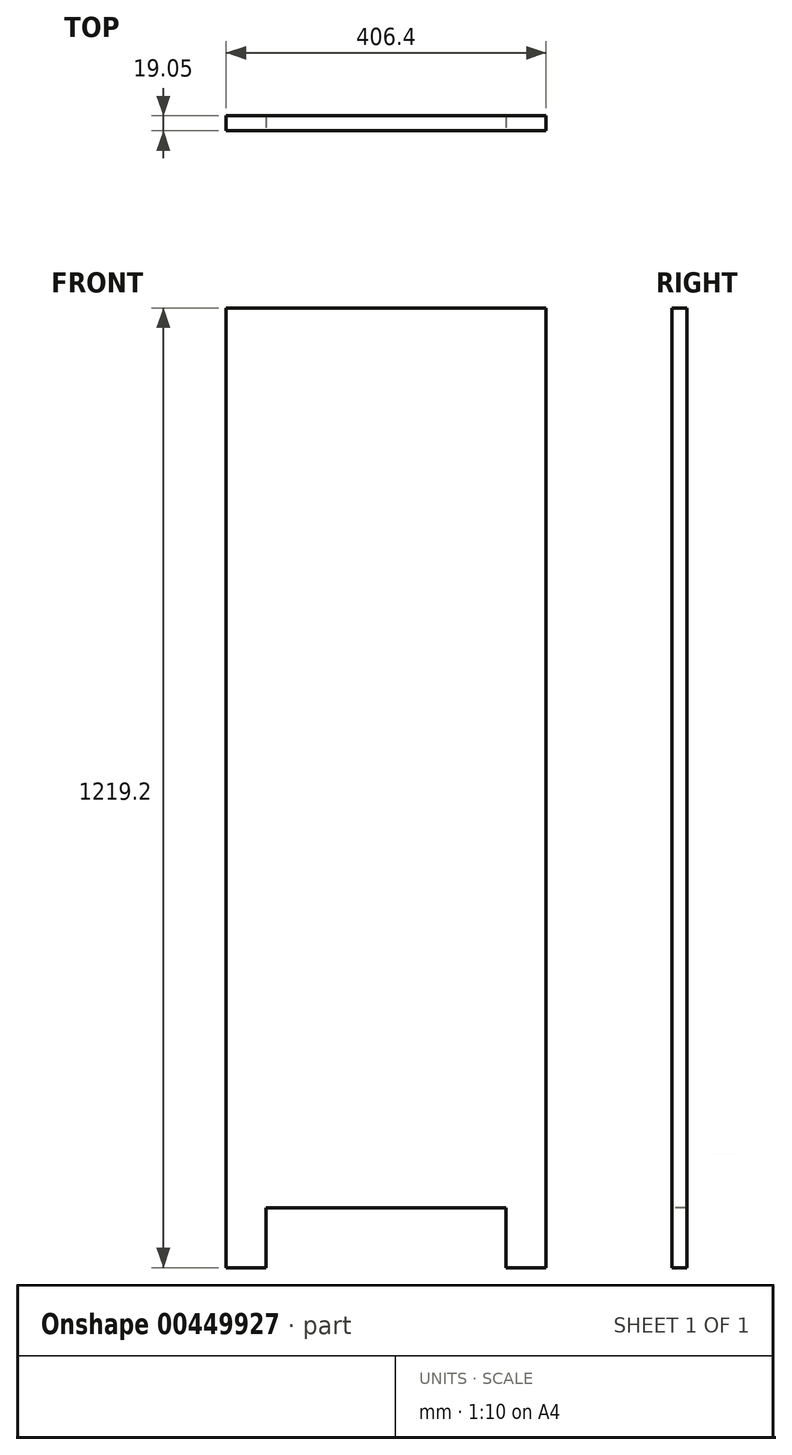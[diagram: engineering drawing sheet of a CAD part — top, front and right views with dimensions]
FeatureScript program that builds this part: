
annotation { "Feature Type Name" : "Feature", "Feature Type Description" : "" }
export const myFeature = defineFeature(function(context is Context, id is Id, definition is map)
    precondition{}
    {
        {
            var Q0;
            Q0=qCreatedBy(makeId("Top.planeOp"),FACE);
            var sketch = newSketch(context, id + "F0", { "sketchPlane" : qUnion([Q0])});
            skLineSegment(sketch, "E0.bottom", {"start": v(0, 0) * mm, "end": v(406.4, 0) * mm});
            skLineSegment(sketch, "E0.top", {"start": v(0, 19.05) * mm, "end": v(406.4, 19.05) * mm});
            skLineSegment(sketch, "E0.left", {"start": v(0, 0) * mm, "end": v(0, 19.05) * mm});
            skLineSegment(sketch, "E0.right", {"start": v(406.4, 0) * mm, "end": v(406.4, 19.05) * mm});
            skSolve(sketch);
        }
        {
            var Q0;
            Q0=makeQuery(id+"F0.imprint","IMPRINT",FACE,{"disambiguationData":[TD([[makeQuery(id+"F0.imprint","IMPRINT",EDGE,{"derivedFrom":sQuery(id+"F0.wireOp",EDGE,"E0.bottom")}),1.0]])]});
            extrude(context, id + "F1", {"entities" : qUnion([Q0]), "depth" : 1219.2 * mm});
        }
        {
            var Q0;
            Q0=makeQuery(id+"F1.opExtrude","SWEPT_FACE",FACE,{"disambiguationData":[OSD([sQuery(id+"F0.wireOp",EDGE,"E0.bottom")])]});
            var sketch = newSketch(context, id + "F2", { "sketchPlane" : qUnion([Q0])});
            skLineSegment(sketch, "E1.bottom", {"start": v(50.8, 0) * mm, "end": v(355.6, 0) * mm});
            skLineSegment(sketch, "E1.top", {"start": v(50.8, 76.2) * mm, "end": v(355.6, 76.2) * mm});
            skLineSegment(sketch, "E1.left", {"start": v(50.8, 0) * mm, "end": v(50.8, 76.2) * mm});
            skLineSegment(sketch, "E1.right", {"start": v(355.6, 0) * mm, "end": v(355.6, 76.2) * mm});
            skLineSegment(sketch, "E2", {"start": v(203.2, 76.2) * mm, "end": v(203.2, 0) * mm, "construction": true});
            skSolve(sketch);
        }
        {
            var Q0;
            Q0=makeQuery(id+"F2.imprint","IMPRINT",FACE,{"disambiguationData":[TD([[makeQuery(id+"F2.imprint","IMPRINT",EDGE,{"derivedFrom":sQuery(id+"F2.wireOp",EDGE,"E1.bottom")}),1.0]])]});
            extrude(context, id + "F3", {"entities" : qUnion([Q0]), "operationType" : NewBodyOperationType.REMOVE, "endBound" : BoundingType.THROUGH_ALL, "oppositeDirection" : true, "depth" : 25.4 * mm});
        }
    });
